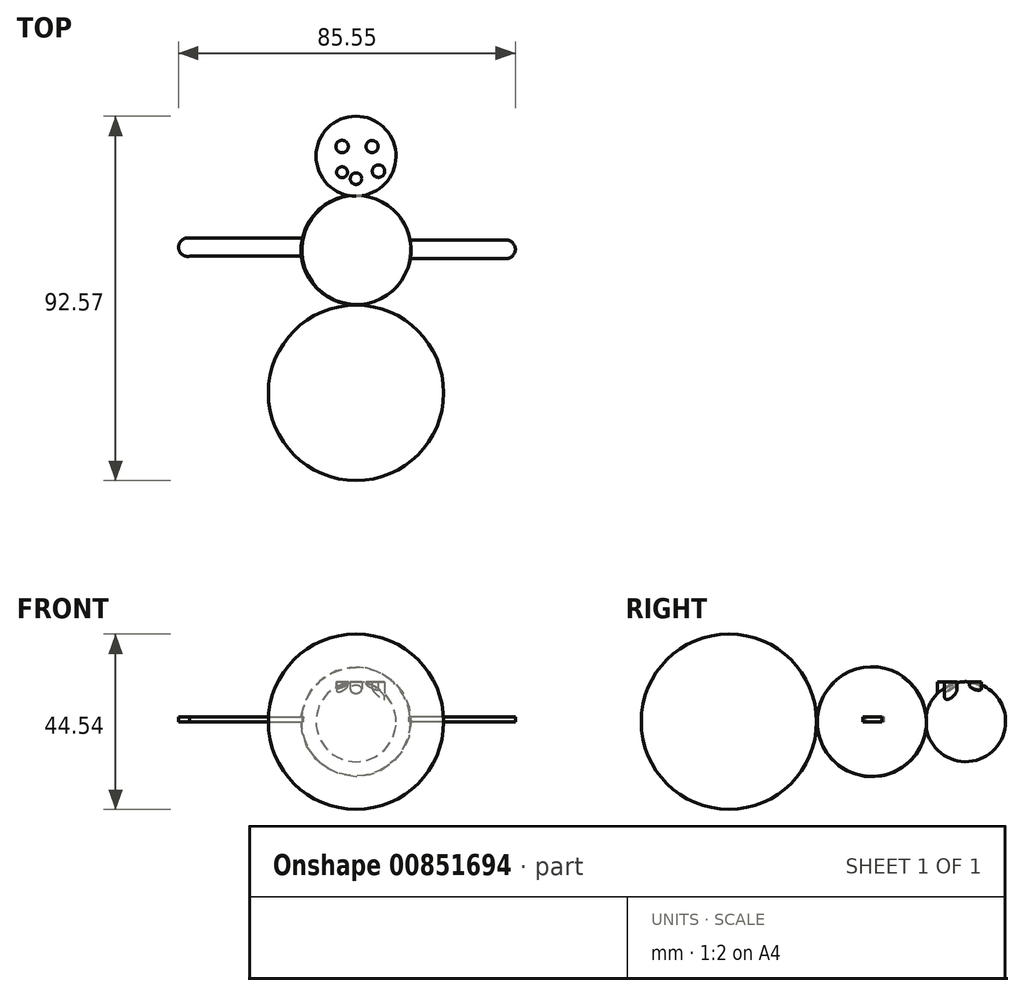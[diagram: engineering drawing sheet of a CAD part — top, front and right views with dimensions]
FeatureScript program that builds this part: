
annotation { "Feature Type Name" : "Feature", "Feature Type Description" : "" }
export const myFeature = defineFeature(function(context is Context, id is Id, definition is map)
    precondition{}
    {
        {
            var Q0;
            Q0=qCreatedBy(makeId("Top.planeOp"),FACE);
            var sketch = newSketch(context, id + "F0", { "sketchPlane" : qUnion([Q0])});
            skArc(sketch, "E0", {"start": v(0, 0) * mm, "mid": v(13.77, 13.87) * mm, "end": v(0, 27.73) * mm});
            skLineSegment(sketch, "E1", {"start": v(0, 27.73) * mm, "end": v(0, 0) * mm});
            skSolve(sketch);
        }
        {
            var Q0;
            Q0=makeQuery(id+"F0.imprint","IMPRINT",FACE,{"disambiguationData":[TD([[makeQuery(id+"F0.imprint","IMPRINT",EDGE,{"derivedFrom":sQuery(id+"F0.wireOp",EDGE,"E0")}),1.0]])]});
            var Q1;
            Q1=sQuery(id+"F0.wireOp",EDGE,"E1");
            revolve(context, id + "F1", {"surfaceOperationType" : NewSurfaceOperationType.NEW, "entities" : qUnion([Q0]), "axis" : qUnion([Q1]), "revolveType" : RevolveType.FULL});
        }
        {
            var Q0;
            Q0=qCreatedBy(makeId("Top.planeOp"),FACE);
            var sketch = newSketch(context, id + "F2", { "sketchPlane" : qUnion([Q0])});
            skCircle(sketch, "E2", {"center": v(0, -22.45) * mm, "radius": 22.27 * mm});
            skLineSegment(sketch, "E3", {"start": v(0, -22.45) * mm, "end": v(0, -44.72) * mm});
            skLineSegment(sketch, "E4", {"start": v(0, -44.72) * mm, "end": v(0, 0) * mm});
            skSolve(sketch);
        }
        {
            var Q0;
            {var subQ0=sQuery(id+"F2.wireOp",EDGE,"E3");Q0=makeQuery(id+"F2.imprint","IMPRINT",FACE,{"disambiguationData":[TD([[makeQuery(id+"F2.imprint","IMPRINT",EDGE,{"derivedFrom":subQ0}),1.0]])]});}
            var Q1;
            Q1=sQuery(id+"F2.wireOp",EDGE,"E4");
            revolve(context, id + "F3", {"surfaceOperationType" : NewSurfaceOperationType.NEW, "entities" : qUnion([Q0]), "axis" : qUnion([Q1]), "revolveType" : RevolveType.FULL});
        }
        {
            var Q0;
            Q0=qCreatedBy(makeId("Top.planeOp"),FACE);
            var sketch = newSketch(context, id + "F4", { "sketchPlane" : qUnion([Q0])});
            skCircle(sketch, "E5", {"center": v(0, 37.7) * mm, "radius": 10.16 * mm});
            skLineSegment(sketch, "E6", {"start": v(0, 47.85) * mm, "end": v(0, 27.53) * mm});
            skSolve(sketch);
        }
        {
            var Q0;
            {var subQ0=sQuery(id+"F4.wireOp",EDGE,"E6");Q0=makeQuery(id+"F4.imprint","IMPRINT",FACE,{"disambiguationData":[TD([[makeQuery(id+"F4.imprint","IMPRINT",EDGE,{"derivedFrom":subQ0}),1.0]])]});}
            var Q1;
            Q1=sQuery(id+"F4.wireOp",EDGE,"E6");
            revolve(context, id + "F5", {"surfaceOperationType" : NewSurfaceOperationType.NEW, "entities" : qUnion([Q0]), "axis" : qUnion([Q1]), "revolveType" : RevolveType.FULL});
        }
        {
            var Q0;
            Q0=qCreatedBy(makeId("Top.planeOp"),FACE);
            var sketch = newSketch(context, id + "F6", { "sketchPlane" : qUnion([Q0])});
            skCircle(sketch, "E7", {"center": v(-42.72, 14.56) * mm, "radius": 2.36 * mm});
            skCircle(sketch, "E8", {"center": v(38.1, 14.02) * mm, "radius": 2.37 * mm});
            skLineSegment(sketch, "E9", {"start": v(-42.72, 16.92) * mm, "end": v(-12.25, 16.92) * mm});
            skLineSegment(sketch, "E10", {"start": v(-42.23, 12.26) * mm, "end": v(-13.06, 12.26) * mm});
            skLineSegment(sketch, "E11", {"start": v(38.1, 16.39) * mm, "end": v(12.8, 16.39) * mm});
            skLineSegment(sketch, "E12", {"start": v(38.1, 11.64) * mm, "end": v(12.25, 11.64) * mm});
            skLineSegment(sketch, "E13", {"start": v(12.8, 16.39) * mm, "end": v(12.25, 11.64) * mm});
            skLineSegment(sketch, "E14", {"start": v(-12.25, 16.92) * mm, "end": v(-13.06, 12.26) * mm});
            skSolve(sketch);
        }
        {
            var Q0;
            Q0 = qSketchRegion(id + "F6", true);
            extrude(context, id + "F7", {"entities" : qUnion([Q0]), "operationType" : NewBodyOperationType.ADD, "depth" : 1.27 * mm, "offsetDistance" : 25.4 * mm});
        }
        {
            var Q0;
            Q0=qCreatedBy(makeId("Top.planeOp"),FACE);
            var sketch = newSketch(context, id + "F8", { "sketchPlane" : qUnion([Q0])});
            skCircle(sketch, "E15", {"center": v(-3.54, 40.14) * mm, "radius": 1.59 * mm});
            skCircle(sketch, "E16", {"center": v(5.72, 33.88) * mm, "radius": 1.59 * mm});
            skCircle(sketch, "E17", {"center": v(4.08, 40.14) * mm, "radius": 1.54 * mm});
            skCircle(sketch, "E18", {"center": v(0, 31.98) * mm, "radius": 1.47 * mm});
            skCircle(sketch, "E19", {"center": v(-3.54, 33.6) * mm, "radius": 1.38 * mm});
            skSolve(sketch);
        }
        {
            var Q0;
            Q0 = qSketchRegion(id + "F8", true);
            extrude(context, id + "F9", {"entities" : qUnion([Q0]), "operationType" : NewBodyOperationType.ADD, "depth" : 10.16 * mm, "offsetDistance" : 25.4 * mm});
        }
        {
            var Q0;
            Q0=qCreatedBy(makeId("Top.planeOp"),FACE);
            var sketch = newSketch(context, id + "F10", { "sketchPlane" : qUnion([Q0])});
            skCircle(sketch, "E20", {"center": v(0, 22.72) * mm, "radius": 1.65 * mm});
            skCircle(sketch, "E21", {"center": v(0, 16.2) * mm, "radius": 1.97 * mm});
            skCircle(sketch, "E22", {"center": v(0, 8.84) * mm, "radius": 1.61 * mm});
            skSolve(sketch);
        }
        {
            var Q0;
            Q0 = qSketchRegion(id + "F10", true);
            extrude(context, id + "F11", {"entities" : qUnion([Q0]), "operationType" : NewBodyOperationType.ADD, "depth" : 7.62 * mm, "offsetDistance" : 25.4 * mm});
        }
    });
